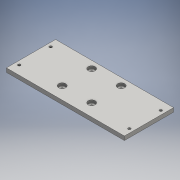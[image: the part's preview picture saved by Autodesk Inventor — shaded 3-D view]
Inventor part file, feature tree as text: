
AUTODESK INVENTOR PART (.ipt)
format: ipt  version: 2016 (Build 200138000, 138)  size: 122,368 bytes
history: native  units: mm
features: sketch x3, hole x2, extrude x1
ambient origin geometry x8: Origin, YZ Plane, XZ Plane, XY Plane, X Axis, Y Axis, Z Axis, Center Point
bodies: Solid1 (feature_tree)
feature tree (6):
  extrude  "Extrusion1"  Depth=300.0mm
  hole  "Hole1"  [1 undecoded]
  hole  "Hole2"  [1 undecoded]
  sketch  "Sketch1"  dims[d0=125.0mm d1=300.0mm]
  sketch  "Sketch2"  dims[d2=150.0mm d3=62.5mm]
  sketch  "Sketch3"  dims[d4=10.0mm d5=0.0mm d6=75.0mm d7=18.475mm d8=75.0mm d9=6.6mm d10=6.0mm d11=18.0mm d12=7.0mm d13=14.3117mm d14=8.0mm d15=20.594885mm d16=80.0mm d17=40.0mm d18=280.0mm d19=140.0mm d20=6.6mm d21=6.0mm d22=18.0mm d23=7.0mm d24=14.3117mm d25=8.0mm d26=20.594885mm]
note: 2 required parameter values undecoded (feature->parameter linkage not recoverable at this tier; creation-order binding heuristic only, values carry confidence <= 0.55)
